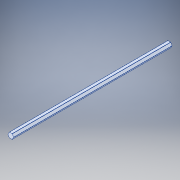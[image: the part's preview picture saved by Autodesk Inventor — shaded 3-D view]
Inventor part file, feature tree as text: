
AUTODESK INVENTOR PART (.ipt)
format: ipt  version: 2017 (Build 210142000, 142)  size: 149,504 bytes
history: native  units: in
note: dims shown in document units (in); Inventor stores cm internally (conversion verified against a paired STEP export)
features: sketch x5, split x1, fillet x1
ambient origin geometry x8: Origin, YZ Plane, XZ Plane, XY Plane, X Axis, Y Axis, Z Axis, Center Point
bodies: Solid1 (feature_tree)
feature tree (7):
  sketch  "Sketch1"  dims[d11=16.0in]
  split  "Split1"
  sketch  "Sketch3"  dims[d13=7.8125in]
  sketch  "Sketch4"  dims[d14=3.5453in]
  sketch  "Sketch5"  dims[d15=3.5453in]
  sketch  "Sketch2"  dims[d12=7.8125in]
  fillet  "Fillet1"  Radius=8.5in
